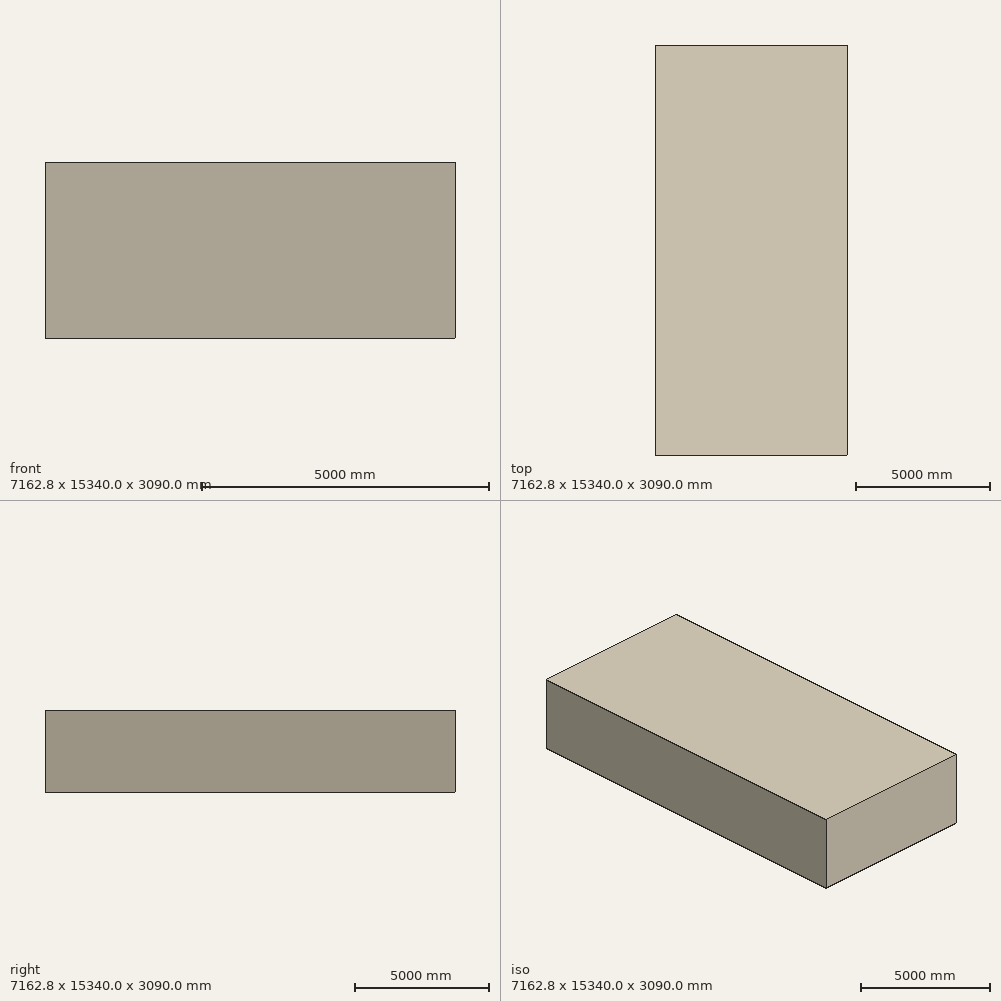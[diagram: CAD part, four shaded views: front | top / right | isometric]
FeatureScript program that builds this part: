
annotation { "Feature Type Name" : "Feature", "Feature Type Description" : "" }
export const myFeature = defineFeature(function(context is Context, id is Id, definition is map)
    precondition{}
    {
        {
            var Q0;
            Q0=qCreatedBy(makeId("Front.planeOp"),FACE);
            var sketch = newSketch(context, id + "F0", { "sketchPlane" : qUnion([Q0])});
            skLineSegment(sketch, "E0.bottom", {"start": v(-3582.4, 928.42) * mm, "end": v(3580.4, 928.42) * mm});
            skLineSegment(sketch, "E0.top", {"start": v(-3582.4, -2161.58) * mm, "end": v(3580.4, -2161.58) * mm});
            skLineSegment(sketch, "E0.left", {"start": v(-3582.4, 928.42) * mm, "end": v(-3582.4, -2161.58) * mm});
            skLineSegment(sketch, "E0.right", {"start": v(3580.4, 928.42) * mm, "end": v(3580.4, -2161.58) * mm});
            skSolve(sketch);
        }
        {
            var Q0;
            Q0 = qSketchRegion(id + "F0", true);
            extrude(context, id + "F1", {"entities" : qUnion([Q0]), "depth" : 15340 * mm});
        }
    });
